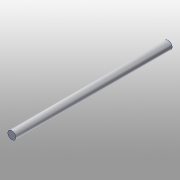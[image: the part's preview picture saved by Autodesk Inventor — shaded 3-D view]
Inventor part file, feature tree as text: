
AUTODESK INVENTOR PART (.ipt)
format: ipt  version: 2016 (Build 200138000, 138)  size: 76,288 bytes
history: native  units: mm
features: extrude x1, sketch x1
ambient origin geometry x8: Origin, YZ Plane, XZ Plane, XY Plane, X Axis, Y Axis, Z Axis, Center Point
bodies: Solid1 (feature_tree)
feature tree (2):
  extrude  "Extrusion1"  Depth=59.0mm TaperAngle=0.0deg
  sketch  "Sketch1"  dims[d0=3.0mm d1=59.0mm d2=0.0mm]
